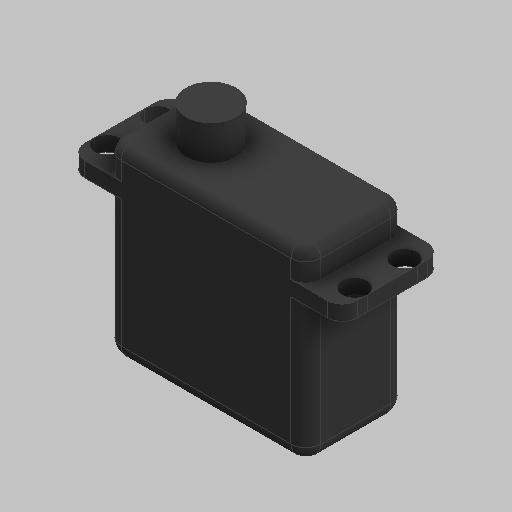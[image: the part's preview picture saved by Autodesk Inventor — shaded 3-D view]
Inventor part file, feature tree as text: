
AUTODESK INVENTOR PART (.ipt)
format: ipt  version: 2025 (Build 290162010, 162A)  size: 239,104 bytes
history: native  units: mm
features: fillet x8, extrude x5, sketch x5, other x2
ambient origin geometry x8: Origin, YZ Plane, XZ Plane, XY Plane, X Axis, Y Axis, Z Axis, Center Point
bodies: Body1 (feature_tree)
feature tree (20):
  other  "Sólido1"
  extrude  "Extrusión1"  Depth=40.0mm
  fillet  "Empalme1"  Radius=10.0mm
  fillet  "Empalme2"  Radius=20.0mm
  fillet  "Empalme3"  Radius=28.5mm
  extrude  "Extrusión2"  Depth=3.0mm
  fillet  "Empalme4"  Radius=3.0mm
  fillet  "Empalme5"  [1 undecoded]
  extrude  "Extrusión3"  Depth=54.5mm
  fillet  "Empalme6"  Radius=27.25mm
  fillet  "Empalme7"  Radius=3.0mm
  fillet  "Empalme8"  Radius=3.0mm
  extrude  "Extrusión4"  Depth=20.0mm
  extrude  "Extrusión5"  Depth=5.7mm TaperAngle=0.0deg
  sketch  "Boceto1"  dims[d0=20.0mm d1=40.0mm d2=10.0mm d3=20.0mm d4=28.5mm d5=0.0mm]
  sketch  "Boceto2"  dims[d6=3.0mm d7=3.0mm d8=3.0mm d9=0.0mm]
  sketch  "Boceto3"  dims[d10=0.0mm d11=54.5mm d12=27.25mm d13=3.0mm d14=0.0mm d15=3.0mm]
  sketch  "Boceto4"  dims[d16=3.0mm d17=20.0mm]
  sketch  "Boceto5"  dims[d18=20.0mm d19=5.7mm d20=0.0mm d21=3.0mm d22=2.0mm d23=3.0mm d24=24.75mm d25=5.0mm d26=5.0mm d27=24.75mm d28=5.0mm d29=0.0mm d30=10.0mm d31=9.0mm d32=7.0mm d33=0.0mm]
  other  "Finish1"
note: 1 required parameter value undecoded (feature->parameter linkage not recoverable at this tier; creation-order binding heuristic only, values carry confidence <= 0.55)
